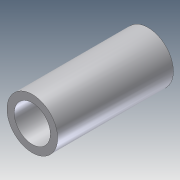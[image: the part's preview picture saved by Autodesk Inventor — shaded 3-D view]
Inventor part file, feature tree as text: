
AUTODESK INVENTOR PART (.ipt)
format: ipt  version: 2012 (Build 160160000, 160)  size: 82,432 bytes
history: native  units: in
note: dims shown in document units (in); Inventor stores cm internally (conversion verified against a paired STEP export)
features: extrude x1, sketch x1
ambient origin geometry x8: Origin, YZ Plane, XZ Plane, XY Plane, X Axis, Y Axis, Z Axis, Center Point
bodies: Solid1 (feature_tree)
feature tree (2):
  extrude  "Extrusion1"  Depth=0.125in
  sketch  "Sketch1"  dims[d0=0.875in d1=0.125in d2=2.0in d3=0.0in]
